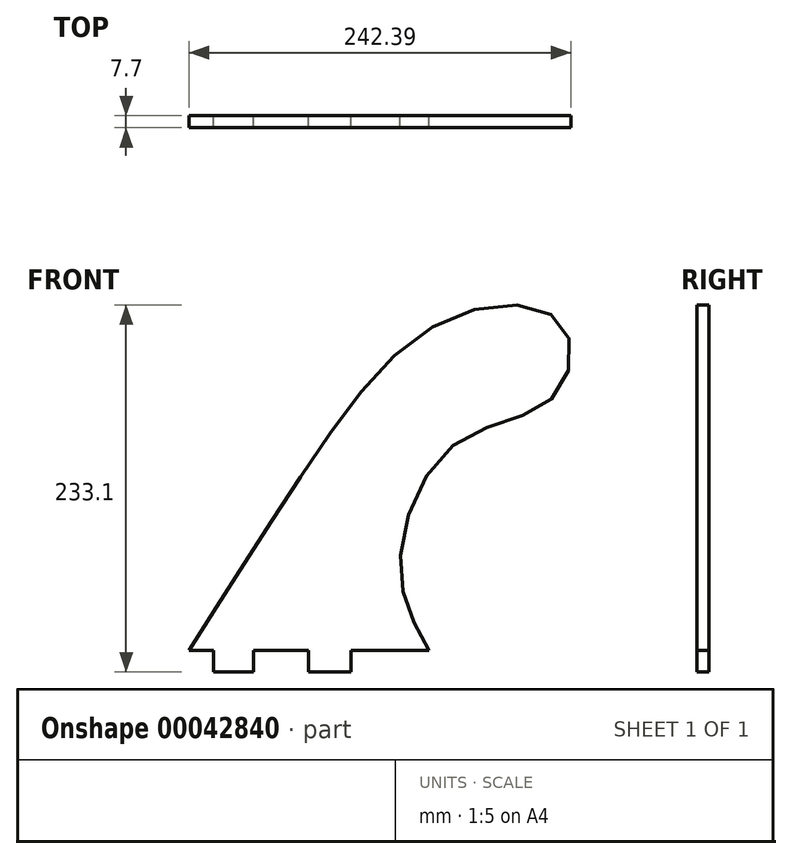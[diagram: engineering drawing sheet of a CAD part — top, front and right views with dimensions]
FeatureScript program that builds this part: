
annotation { "Feature Type Name" : "Feature", "Feature Type Description" : "" }
export const myFeature = defineFeature(function(context is Context, id is Id, definition is map)
    precondition{}
    {
        {
            var Q0;
            Q0=qCreatedBy(makeId("Front.planeOp"),FACE);
            var sketch = newSketch(context, id + "F0", { "sketchPlane" : qUnion([Q0])});
            skLineSegment(sketch, "E0", {"start": v(-75.86, -44.64) * mm, "end": v(-60.5, -44.64) * mm});
            skLineSegment(sketch, "E1", {"start": v(-60.5, -44.64) * mm, "end": v(-60.5, -58.38) * mm});
            skLineSegment(sketch, "E2", {"start": v(-60.5, -58.38) * mm, "end": v(-34.91, -58.38) * mm});
            skLineSegment(sketch, "E3", {"start": v(-34.91, -58.38) * mm, "end": v(-34.91, -44.64) * mm});
            skLineSegment(sketch, "E4", {"start": v(-34.91, -44.64) * mm, "end": v(0, -44.64) * mm});
            skLineSegment(sketch, "E5", {"start": v(0, -44.64) * mm, "end": v(0, -58.38) * mm});
            skLineSegment(sketch, "E6", {"start": v(0, -58.38) * mm, "end": v(26.79, -58.38) * mm});
            skLineSegment(sketch, "E7", {"start": v(26.79, -58.38) * mm, "end": v(26.79, -44.64) * mm});
            skLineSegment(sketch, "E8", {"start": v(26.79, -44.64) * mm, "end": v(76.36, -44.64) * mm});
            skFitSpline(sketch, "E9", {"points": [v(76.36, -44.64) * mm, v(58.04, 8.43) * mm, v(92.8, 86.3) * mm, v(155.03, 115.66) * mm, v(160.69, 162.8) * mm, v(88.21, 165.77) * mm, v(0, 73.36) * mm, v(-75.86, -44.64) * mm], "startDerivative": vector(-229.43, 402.57) * mm, "endDerivative": vector(-398.23, -631.18) * mm});
            skSolve(sketch);
        }
        {
            var Q0;
            Q0=makeQuery(id+"F0.imprint","IMPRINT",FACE,{"disambiguationData":[TD([[makeQuery(id+"F0.imprint","IMPRINT",EDGE,{"derivedFrom":sQuery(id+"F0.wireOp",EDGE,"E0")}),1.0]])]});
            extrude(context, id + "F1", {"entities" : qUnion([Q0]), "depth" : 7.7 * mm});
        }
    });
